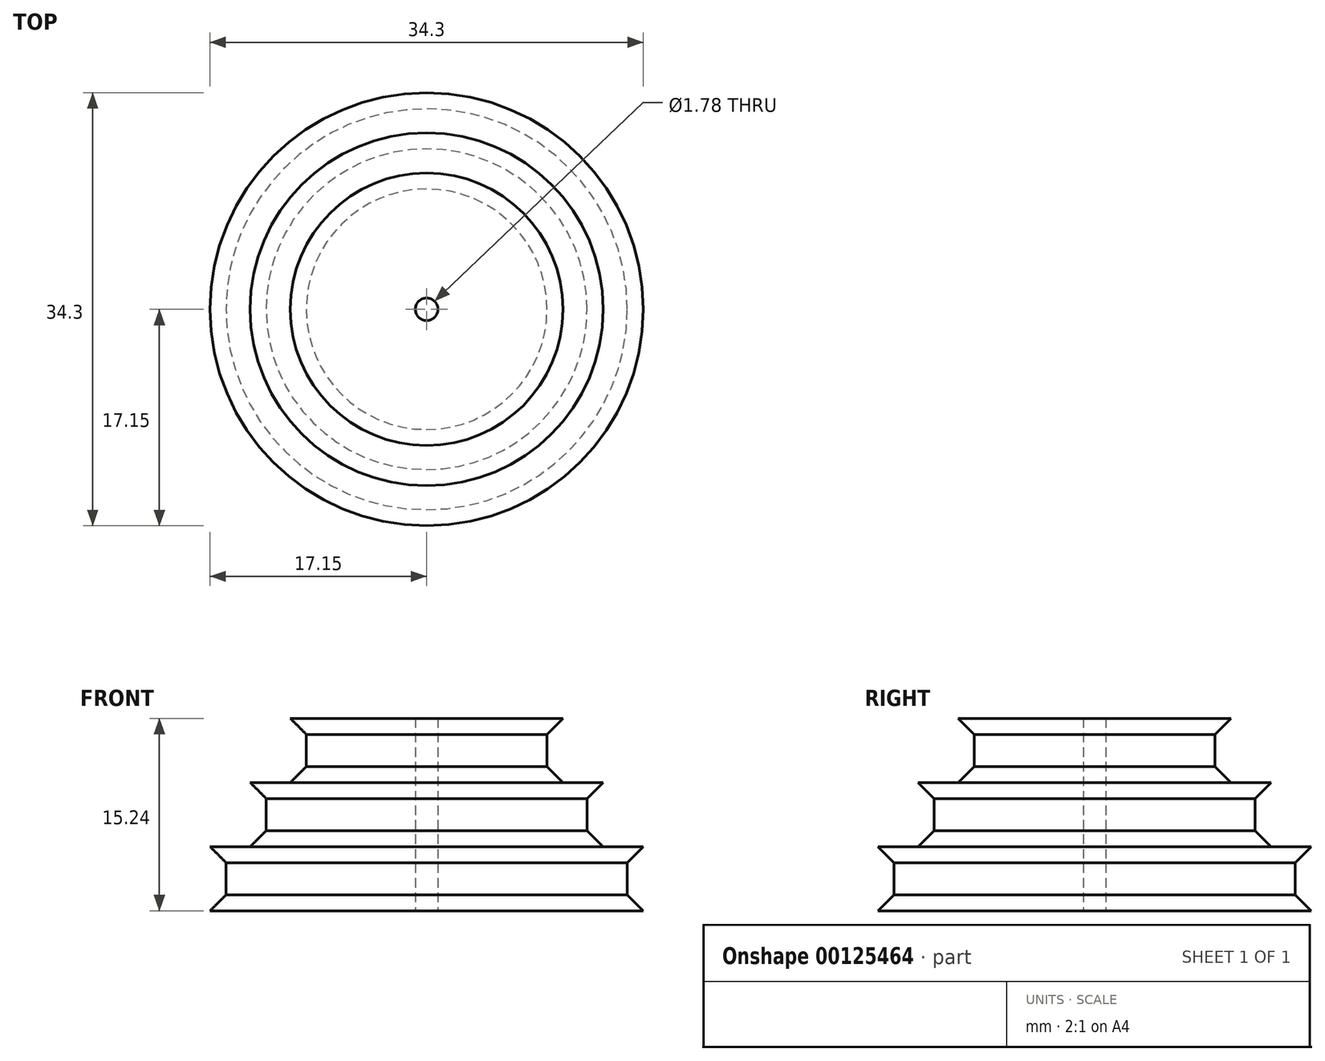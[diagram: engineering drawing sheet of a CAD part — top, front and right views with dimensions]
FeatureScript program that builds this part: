
annotation { "Feature Type Name" : "Feature", "Feature Type Description" : "" }
export const myFeature = defineFeature(function(context is Context, id is Id, definition is map)
    precondition{}
    {
        {
            var Q0;
            Q0=qCreatedBy(makeId("Front.planeOp"),FACE);
            var sketch = newSketch(context, id + "F0", { "sketchPlane" : qUnion([Q0])});
            skLineSegment(sketch, "E0", {"start": v(0, 0) * mm, "end": v(0, 70.31) * mm, "construction": true});
            skLineSegment(sketch, "E1", {"start": v(-0.89, 0) * mm, "end": v(-0.89, 15.24) * mm});
            skLineSegment(sketch, "E2", {"start": v(-0.89, 15.24) * mm, "end": v(-10.8, 15.24) * mm});
            skLineSegment(sketch, "E3", {"start": v(-10.8, 15.24) * mm, "end": v(-9.53, 13.97) * mm});
            skLineSegment(sketch, "E4", {"start": v(-9.53, 13.97) * mm, "end": v(-9.53, 11.43) * mm});
            skLineSegment(sketch, "E5", {"start": v(-9.53, 11.43) * mm, "end": v(-10.8, 10.16) * mm});
            skLineSegment(sketch, "E6", {"start": v(-10.8, 10.16) * mm, "end": v(-13.97, 10.16) * mm});
            skLineSegment(sketch, "E7", {"start": v(-13.97, 10.16) * mm, "end": v(-12.7, 8.9) * mm});
            skLineSegment(sketch, "E8", {"start": v(-12.7, 8.9) * mm, "end": v(-12.7, 6.35) * mm});
            skLineSegment(sketch, "E9", {"start": v(-12.7, 6.35) * mm, "end": v(-13.97, 5.08) * mm});
            skLineSegment(sketch, "E10", {"start": v(-13.97, 5.08) * mm, "end": v(-17.14, 5.08) * mm});
            skLineSegment(sketch, "E11", {"start": v(-17.14, 5.08) * mm, "end": v(-15.87, 3.81) * mm});
            skLineSegment(sketch, "E12", {"start": v(-15.88, 3.81) * mm, "end": v(-15.88, 1.27) * mm});
            skLineSegment(sketch, "E13", {"start": v(-15.87, 1.27) * mm, "end": v(-17.14, 0) * mm});
            skLineSegment(sketch, "E14", {"start": v(-17.14, 0) * mm, "end": v(-0.89, 0) * mm});
            skSolve(sketch);
        }
        {
            var Q0;
            Q0=makeQuery(id+"F0.imprint","IMPRINT",FACE,{"disambiguationData":[TD([[makeQuery(id+"F0.imprint","IMPRINT",EDGE,{"derivedFrom":sQuery(id+"F0.wireOp",EDGE,"E1")}),1.0]])]});
            var Q1;
            Q1=sQuery(id+"F0.wireOp",EDGE,"E0");
            revolve(context, id + "F1", {"entities" : qUnion([Q0]), "axis" : qUnion([Q1]), "revolveType" : RevolveType.FULL});
        }
    });
